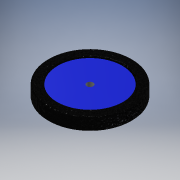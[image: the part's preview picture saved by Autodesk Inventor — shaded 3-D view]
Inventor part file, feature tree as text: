
AUTODESK INVENTOR PART (.ipt)
format: ipt  version: 2017 (Build 210142000, 142)  size: 158,208 bytes
history: native  units: mm
features: revolve x1, sketch x1
ambient origin geometry x8: Origin, YZ Plane, XZ Plane, XY Plane, X Axis, Y Axis, Z Axis, Center Point
bodies: Solid1 (feature_tree)
feature tree (2):
  revolve  "Revolution1"  [1 undecoded]
  sketch  "Sketch1"  dims[d0=560.317934mm d1=40.0mm d2=30.0mm d3=30.0mm d4=260.0mm d5=2.0mm d6=5.0mm d7=20.0mm d8=90.0deg]
note: 1 required parameter value undecoded (feature->parameter linkage not recoverable at this tier; creation-order binding heuristic only, values carry confidence <= 0.55)
